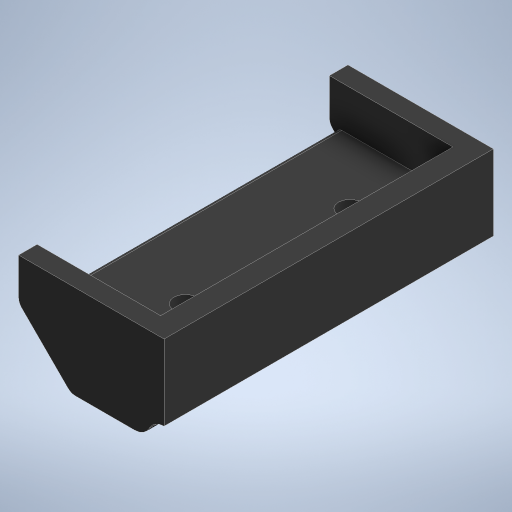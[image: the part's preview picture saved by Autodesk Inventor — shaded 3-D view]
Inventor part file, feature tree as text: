
AUTODESK INVENTOR PART (.ipt)
format: ipt  version: 2024 (Build 280153000, 153)  size: 293,376 bytes
history: native  units: in
note: dims shown in document units (in); Inventor stores cm internally (conversion verified against a paired STEP export)
features: extrude x5, sketch x5, fillet x3, projected_geometry x3
ambient origin geometry x8: Origin, YZ Plane, XZ Plane, XY Plane, X Axis, Y Axis, Z Axis, Center Point
bodies: Solid1 (feature_tree)
feature tree (16):
  extrude  "Extrusion1"  Depth=0.44in
  extrude  "Extrusion2"  Depth=8.0in TaperAngle=0.0deg
  extrude  "Extrusion3"  Depth=0.4in
  extrude  "Extrusion4"  Depth=3.0in
  fillet  "Fillet1"  Radius=0.22in
  fillet  "Fillet2"  Radius=8.0in
  fillet  "Fillet3"  Radius=3.0in
  extrude  "Extrusion5"  Depth=7.1in
  sketch  "Sketch1"  dims[d1=0.44in d2=0.44in]
  sketch  "Sketch2"  dims[d3=0.4in d4=8.0in d5=0.0in]
  sketch  "Sketch3"  dims[d6=2.7in d7=0.4in]
  projected_geometry  "Projected Loop1"
  sketch  "Sketch4"  dims[d9=1.8in d11=0.22in d12=0.22in d13=8.0in d14=0.0in d15=3.0in]
  projected_geometry  "Projected Loop2"
  sketch  "Sketch5"  dims[d16=3.55in d17=7.1in d18=1.0in d19=0.0in d20=0.55in d21=0.55in d22=0.75in d23=0.0in d24=0.125in d25=0.25in d26=0.25in d27=0.25in d28=0.25in d29=1.0in d30=0.0in]
  projected_geometry  "Projected Loop3"
